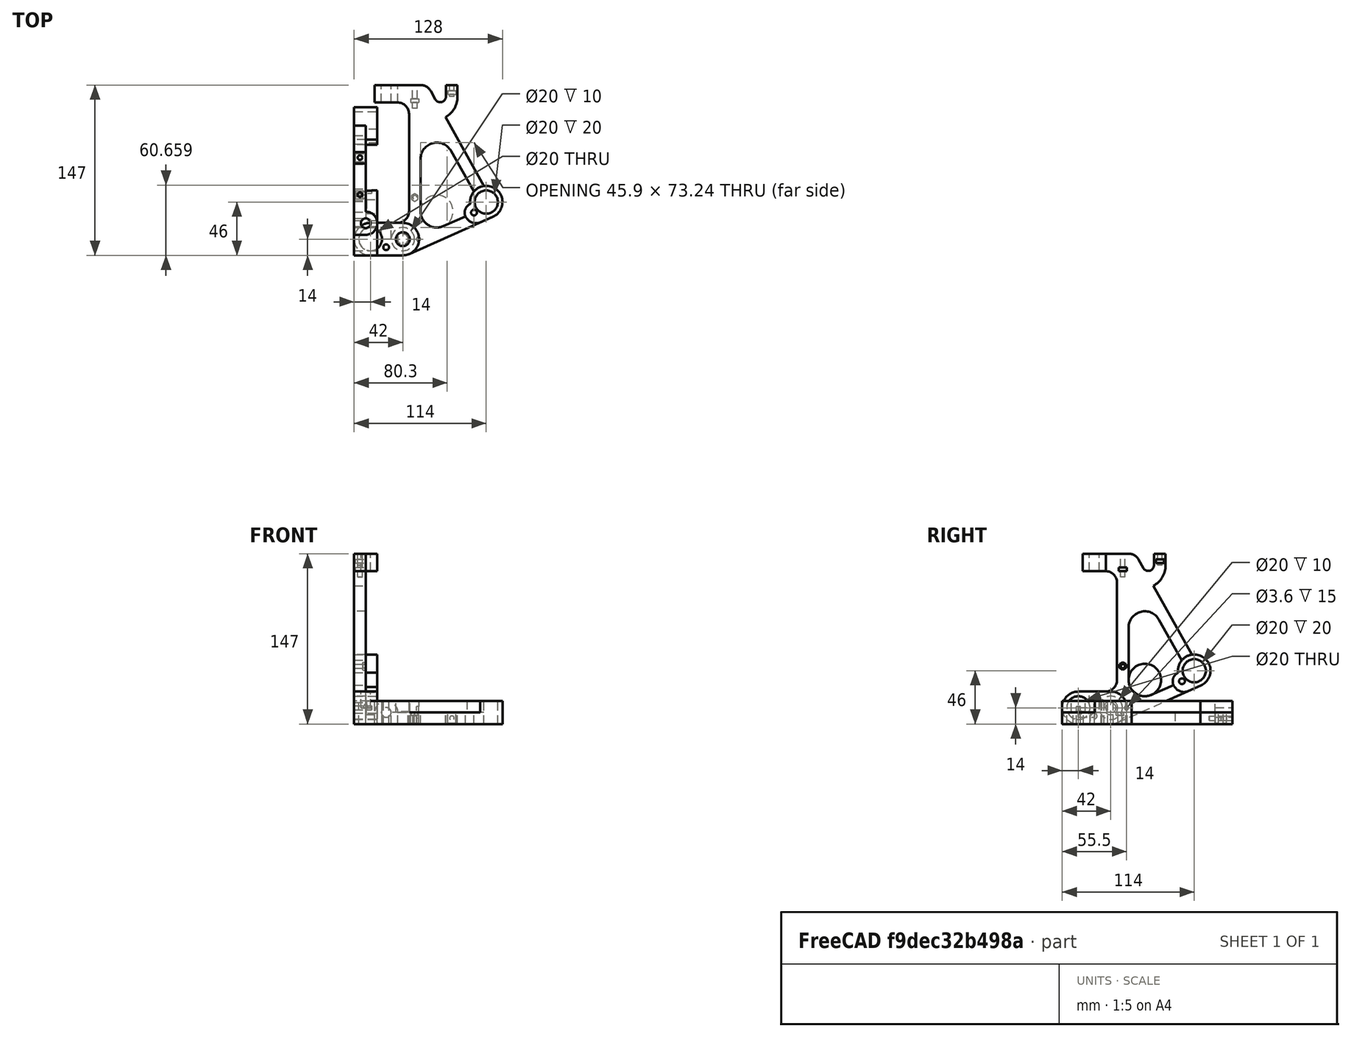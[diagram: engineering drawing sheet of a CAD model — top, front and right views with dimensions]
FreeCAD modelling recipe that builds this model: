
FCSTD DOCUMENT  (FreeCAD 0.15R4527 (Git))
Label: x_carriage_left
License: All rights reserved
LicenseURL: http://en.wikipedia.org/wiki/All_rights_reserved
objects: Part::Cylinder×14, Part::MultiFuse×10, Part::Cut×7, Part::Feature×2, Sketcher::SketchObject×2, Part::Box×2, Mesh::Feature×1, Part::Extrusion×1, PartDesign::Pocket×1, Part::Prism×1
note: 41 computed .brp shape members not serialized (recipe doc carries the construction recipe); baked Part::Feature solids carry a one-line shape summary decoded from their .brp

FEATURE [Mesh::Feature] Xcariageleft
FEATURE [Part::Feature] Xcariageleft001001  label="Xcariageleft002"
  shape: bbox 128 x 147 x 20 mm, 1927 faces, 0 solids (baked)
FEATURE [Sketcher::SketchObject] Sketch
  ExternalGeometry = -> [Xcariageleft001001]
  Placement = pos=(0,0,3.8147e-06) rot=(1,0,0;3.14159rad)
  Support = -> Xcariageleft001001 [Face866]
  sketch-geometry (27):
    g0: LineSegment StartX=14 StartY=-3e-12 StartZ=0 EndX=42 EndY=1e-12 EndZ=0
    g1: LineSegment StartX=47.6883 StartY=-1.20767 StartZ=0 EndX=119.688 EndY=-33.2233 EndZ=0
    g2: LineSegment StartX=111.977 StartY=-59.8687 StartZ=0 EndX=78.7678 EndY=-119.207 EndZ=0
    g3: LineSegment StartX=83.5669 StartY=-90.1556 StartZ=0 EndX=103.25 EndY=-54.9849 EndZ=0
    g4: LineSegment StartX=96.0562 StartY=-33.6591 StartZ=0 EndX=77.0383 EndY=-25.2025 EndZ=0
    g5: LineSegment StartX=57.35 StartY=-37.9949 StartZ=0 EndX=57.35 EndY=-83.3184 EndZ=0
    g6: LineSegment StartX=14 StartY=-28 StartZ=0 EndX=37.35 EndY=-28 EndZ=0
    g7: LineSegment StartX=47.35 StartY=-38 StartZ=0 EndX=47.35 EndY=-122 EndZ=0
    g8: LineSegment StartX=37.35 StartY=-132 StartZ=0 EndX=17.7 EndY=-132 EndZ=0
    g9: ArcOfCircle CenterX=114 CenterY=-46.0156 CenterZ=0 NormalX=0 NormalY=0 NormalZ=1 Radius=14 StartAngle=4.56737 EndAngle=7.43558
    g10: ArcOfCircle CenterX=103.366 CenterY=-36.9095 CenterZ=0 NormalX=0 NormalY=0 NormalZ=1 Radius=8.00001 StartAngle=2.72319 EndAngle=4.29398
    g11: ArcOfCircle CenterX=114 CenterY=-46.0156 CenterZ=0 NormalX=0 NormalY=0 NormalZ=1 Radius=14 StartAngle=3.01294 EndAngle=3.83695
    g12: ArcOfCircle CenterX=71.35 CenterY=-83.3184 CenterZ=0 NormalX=0 NormalY=0 NormalZ=1 Radius=14 StartAngle=3.14159 EndAngle=5.77296
    g13: ArcOfCircle CenterX=68.8096 CenterY=-137 CenterZ=0 NormalX=0 NormalY=0 NormalZ=1 Radius=20.3904 StartAngle=2.53065e-07 EndAngle=1.06057
    g14: ArcOfCircle CenterX=74.3581 CenterY=-137 CenterZ=0 NormalX=0 NormalY=0 NormalZ=1 Radius=4.84187 StartAngle=1.80253e-06 EndAngle=2.63136
    g15: ArcOfCircle CenterX=57.35 CenterY=-137 CenterZ=0 NormalX=0 NormalY=0 NormalZ=1 Radius=10 StartAngle=4.71239 EndAngle=5.77295
    g16: ArcOfCircle CenterX=37.35 CenterY=-122 CenterZ=0 NormalX=0 NormalY=0 NormalZ=1 Radius=10 StartAngle=4.71239 EndAngle=6.28318
    g17: ArcOfCircle CenterX=71.35 CenterY=-37.9949 CenterZ=0 NormalX=0 NormalY=0 NormalZ=1 Radius=14 StartAngle=1.15239 EndAngle=3.14159
    g18: ArcOfCircle CenterX=37.35 CenterY=-38 CenterZ=0 NormalX=0 NormalY=0 NormalZ=1 Radius=10 StartAngle=6.16e-10 EndAngle=1.5708
    g19: ArcOfCircle CenterX=42 CenterY=-13.9999 CenterZ=0 NormalX=0 NormalY=0 NormalZ=1 Radius=13.9999 StartAngle=1.15239 EndAngle=1.5708
    g20: ArcOfCircle CenterX=14 CenterY=-14 CenterZ=0 NormalX=0 NormalY=0 NormalZ=1 Radius=14 StartAngle=1.5708 EndAngle=4.71239
    g21: LineSegment StartX=17.7 StartY=-132 StartZ=0 EndX=17.7 EndY=-147 EndZ=0
    g22: LineSegment StartX=17.7 StartY=-147 StartZ=0 EndX=57.35 EndY=-147 EndZ=0
    g23: LineSegment StartX=70.133 StartY=-134.635 StartZ=0 EndX=66.0763 EndY=-141.884 EndZ=0
    g24: LineSegment StartX=79.2 StartY=-137 StartZ=0 EndX=79.2 EndY=-147 EndZ=0
    g25: LineSegment StartX=89.2 StartY=-137 StartZ=0 EndX=89.2 EndY=-147 EndZ=0
    g26: LineSegment StartX=79.2 StartY=-147 StartZ=0 EndX=89.2 EndY=-147 EndZ=0
  constraints (66):
    c: Coincident(g0,g-4)
    c: Coincident(g0,g-4)
    c: Coincident(g1,g-3)
    c: Coincident(g1,g-3)
    c: Coincident(g2,g-9)
    c: Coincident(g2,g-9)
    c: Coincident(g3,g-8)
    c: Coincident(g3,g-8)
    c: Coincident(g4,g-17)
    c: Coincident(g4,g-17)
    c: Coincident(g5,g-7)
    c: Coincident(g5,g-7)
    c: Coincident(g6,g-5)
    c: Coincident(g6,g-5)
    c: Coincident(g7,g-6)
    c: Coincident(g7,g-6)
    c: Coincident(g8,g-16)
    c: Coincident(g8,g-16)
    c: Coincident(g9,g2)
    c: Coincident(g9,g1)
    c: PointOnObject(g-22,g9)
    c: Coincident(g10,g-20)
    c: Coincident(g10,g4)
    c: PointOnObject(g-19,g10)
    c: Coincident(g11,g10)
    c: Coincident(g11,g3)
    c: PointOnObject(g-21,g11)
    c: Coincident(g12,g5)
    c: Coincident(g12,g3)
    c: PointOnObject(g-27,g12)
    c: Coincident(g13,g2)
    c: Coincident(g13,g-10)
    c: PointOnObject(g-23,g13)
    c: Coincident(g14,g-13)
    c: Coincident(g14,g-12)
    c: PointOnObject(g-24,g14)
    c: Coincident(g15,g-13)
    c: Coincident(g15,g-14)
    c: PointOnObject(g-25,g15)
    c: Coincident(g16,g8)
    c: Coincident(g16,g7)
    c: PointOnObject(g-26,g16)
    c: Coincident(g17,g5)
    c: Coincident(g17,g4)
    c: PointOnObject(g-18,g17)
    c: Coincident(g18,g7)
    c: Coincident(g18,g6)
    c: PointOnObject(g-28,g18)
    c: Coincident(g19,g1)
    c: Coincident(g19,g0)
    c: PointOnObject(g-30,g19)
    c: Coincident(g20,g6)
    c: Coincident(g20,g0)
    c: PointOnObject(g-29,g20)
    c: Coincident(g21,g8)
    c: Coincident(g21,g-15)
    c: Coincident(g22,g21)
    c: Coincident(g22,g15)
    c: Coincident(g23,g14)
    c: Coincident(g23,g15)
    c: Coincident(g24,g14)
    c: Coincident(g24,g-12)
    c: Coincident(g25,g13)
    c: Coincident(g25,g-11)
    c: Coincident(g26,g24)
    c: Coincident(g26,g25)
FEATURE [Part::Cylinder] Cylinder  label="Cilindro"
  Angle = 360
  Height = 15
  Placement = pos=(27.7,132,10) rot=(-1,0,0;1.5708rad)
  Radius = 10
FEATURE [Part::Cylinder] Cylinder001  label="rod_hole"
  Angle = 360
  Height = 15
  Placement = pos=(27.7,132,10) rot=(-1,0,0;1.5708rad)
  Radius = 4.2
FEATURE [Part::Cylinder] Cylinder002  label="Cilindro001"
  Angle = 360
  Height = 22
  Placement = pos=(14,14,-1) rot=(0,0,1;0rad)
  Radius = 10
FEATURE [Part::Cylinder] Cylinder003  label="Cilindro002"
  Angle = 360
  Height = 22
  Placement = pos=(114,46,-1) rot=(0,0,1;0rad)
  Radius = 10
FEATURE [Part::Cylinder] Cylinder004  label="Cilindro003"
  Angle = 360
  Height = 10
  Placement = pos=(42,14,10.6) rot=(0,0,1;0rad)
  Radius = 6
FEATURE [Part::Cylinder] Cylinder005  label="Cilindro004"
  Angle = 360
  Height = 11
  Placement = pos=(42,14,-1) rot=(0,0,1;0rad)
  Radius = 10
FEATURE [Part::Cylinder] Cylinder006  label="threaded_rod"
  Angle = 360
  Height = 10
  Placement = pos=(42,14,0) rot=(0,0,1;0rad)
  Radius = 4.5
FEATURE [Part::MultiFuse] Fusion003  label="bearing_holes"
  Shapes = -> [Cylinder002,Cylinder003]
FEATURE [Part::MultiFuse] Fusion004  label="threaded_rod_holes"
  Shapes = -> [Cylinder004,Cylinder005]
FEATURE [Part::Extrusion] Extrude
  Base = -> Sketch
  Dir = (0,0,20)
  Solid = true
FEATURE [Sketcher::SketchObject] Sketch001
  ExternalGeometry = -> [Extrude]
  Placement = pos=(0,0,20) rot=(0,0,1;0rad)
  Support = -> Extrude [Face29]
  sketch-geometry (31):
    g0: LineSegment StartX=37.35 StartY=132 StartZ=0 EndX=17.7 EndY=132 EndZ=0
    g1: LineSegment StartX=17.7 StartY=132 StartZ=0 EndX=17.7 EndY=147 EndZ=0
    g2: LineSegment StartX=17.7 StartY=147 StartZ=0 EndX=57.35 EndY=147 EndZ=0
    g3: LineSegment StartX=79.2 StartY=137 StartZ=0 EndX=79.2 EndY=147 EndZ=0
    g4: LineSegment StartX=89.2 StartY=147 StartZ=0 EndX=89.2 EndY=137 EndZ=0
    g5: ArcOfCircle CenterX=57.35 CenterY=137 CenterZ=0 NormalX=0 NormalY=0 NormalZ=1 Radius=10 StartAngle=0.510231 EndAngle=1.5708
    g6: ArcOfCircle CenterX=68.8096 CenterY=137 CenterZ=0 NormalX=0 NormalY=0 NormalZ=1 Radius=20.3904 StartAngle=5.22262 EndAngle=6.28319
    g7: ArcOfCircle CenterX=74.3581 CenterY=137 CenterZ=0 NormalX=0 NormalY=0 NormalZ=1 Radius=4.84187 StartAngle=3.65182 EndAngle=6.28318
    g8: LineSegment StartX=66.0763 StartY=141.884 StartZ=0 EndX=70.133 EndY=134.635 EndZ=0
    g9: ArcOfCircle CenterX=37.35 CenterY=122 CenterZ=0 NormalX=0 NormalY=0 NormalZ=1 Radius=10 StartAngle=1.08019e-06 EndAngle=1.5708
    g10: LineSegment StartX=79.2 StartY=147 StartZ=0 EndX=89.2 EndY=147 EndZ=0
    g11: LineSegment StartX=47.35 StartY=122 StartZ=0 EndX=47.35 EndY=38 EndZ=0
    g12: LineSegment StartX=57.35 StartY=83.3184 StartZ=0 EndX=57.35 EndY=37.9949 EndZ=0
    g13: ArcOfCircle CenterX=71.35 CenterY=83.3184 CenterZ=0 NormalX=0 NormalY=0 NormalZ=1 Radius=14 StartAngle=0.510228 EndAngle=3.14159
    g14: LineSegment StartX=83.5669 StartY=90.1556 StartZ=0 EndX=103.25 EndY=54.9849 EndZ=0
    g15: LineSegment StartX=77.0383 StartY=25.2025 StartZ=0 EndX=96.0562 EndY=33.6591 EndZ=0
    g16: LineSegment [constr] StartX=57.35 StartY=37.9949 StartZ=0 EndX=71.35 EndY=37.9949 EndZ=0
    g17: LineSegment [constr] StartX=71.35 StartY=37.9949 StartZ=0 EndX=77.0383 EndY=25.2025 EndZ=0
    g18: ArcOfCircle CenterX=71.35 CenterY=37.9949 CenterZ=0 NormalX=0 NormalY=0 NormalZ=1 Radius=14 StartAngle=3.14159 EndAngle=5.13079
    g19: LineSegment [constr] StartX=111.977 StartY=59.8687 StartZ=0 EndX=114 EndY=46.0156 EndZ=0
    g20: ArcOfCircle CenterX=114 CenterY=46.0156 CenterZ=0 NormalX=0 NormalY=0 NormalZ=1 Radius=14 StartAngle=1.71582 EndAngle=2.44623
    g21: LineSegment [constr] StartX=103.366 StartY=36.9095 StartZ=0 EndX=96.0562 EndY=33.6591 EndZ=0
    g22: LineSegment StartX=111.977 StartY=59.8687 StartZ=0 EndX=78.7678 EndY=119.207 EndZ=0
    g23: LineSegment [constr] StartX=119.688 StartY=33.2233 StartZ=0 EndX=108.723 EndY=28.3476 EndZ=0
    g24: ArcOfCircle CenterX=41.9997 CenterY=13.9999 CenterZ=0 NormalX=0 NormalY=0 NormalZ=1 Radius=14.0001 StartAngle=5.13081 EndAngle=7.85396
    g25: LineSegment StartX=37.35 StartY=28 StartZ=0 EndX=42 EndY=28 EndZ=0
    g26: LineSegment [constr] StartX=37.35 StartY=28 StartZ=0 EndX=41.9997 EndY=13.9999 EndZ=0
    g27: ArcOfCircle CenterX=37.35 CenterY=38 CenterZ=0 NormalX=0 NormalY=0 NormalZ=1 Radius=10 StartAngle=4.71239 EndAngle=6.28319
    g28: LineSegment StartX=47.6883 StartY=1.20767 StartZ=0 EndX=108.723 EndY=28.3476 EndZ=0
    g29: ArcOfCircle CenterX=103.366 CenterY=36.9095 CenterZ=0 NormalX=0 NormalY=0 NormalZ=1 Radius=8 StartAngle=3.56 EndAngle=3.8283
    g30: ArcOfCircle CenterX=105.144 CenterY=37.344 CenterZ=0 NormalX=0 NormalY=0 NormalZ=1 Radius=9.68242 StartAngle=3.74652 EndAngle=5.09109
  constraints (78):
    c: Coincident(g0,g-14)
    c: Coincident(g0,g-5)
    c: Coincident(g1,g0)
    c: Coincident(g1,g-6)
    c: Coincident(g2,g1)
    c: Coincident(g2,g-8)
    c: Coincident(g3,g-10)
    c: Coincident(g3,g-11)
    c: Coincident(g4,g-12)
    c: Coincident(g4,g-13)
    c: Coincident(g5,g-8)
    c: Coincident(g5,g2)
    c: Coincident(g5,g-8)
    c: Coincident(g6,g-13)
    c: Coincident(g6,g4)
    c: Coincident(g6,g-15)
    c: Coincident(g7,g-9)
    c: Coincident(g7,g-9)
    c: Coincident(g7,g3)
    c: Coincident(g8,g5)
    c: Coincident(g8,g7)
    c: Coincident(g9,g-14)
    c: Coincident(g9,g0)
    c: Coincident(g9,g-14)
    c: Coincident(g10,g3)
    c: Coincident(g10,g4)
    c: Coincident(g11,g9)
    c: Coincident(g11,g-19)
    c: Coincident(g12,g-18)
    c: Coincident(g13,g-17)
    c: Coincident(g13,g12)
    c: Coincident(g13,g-17)
    c: Coincident(g14,g13)
    c: Coincident(g15,g-21)
    c: Coincident(g16,g12)
    c: Horizontal(g16)
    c: Coincident(g17,g16)
    c: Coincident(g17,g15)
    c: DistanceX(g16) = 14
    c: Equal(g16,g17)
    c: Vertical(g12)
    c: Coincident(g18,g16)
    c: Coincident(g18,g12)
    c: Coincident(g18,g15)
    c: Distance(g19) = 14
    c: Coincident(g20,g19)
    c: Coincident(g20,g19)
    c: Coincident(g19,g-15)
    c: Coincident(g21,g15)
    c: Parallel(g21,g-21)
    c: Distance(g21) = 8
    c: Coincident(g15,g-21)
    c: Coincident(g14,g-16)
    c: Coincident(g22,g19)
    c: Coincident(g22,g6)
    c: Coincident(g23,g-20)
    c: Distance(g23) = 12
    c: PointOnObject(g23,g-20)
    c: Coincident(g25,g-19)
    c: Coincident(g25,g24)
    c: Horizontal(g25)
    c: DistanceX(g25) = 4.65003
    c: Coincident(g26,g25)
    c: Coincident(g26,g24)
    c: Distance(g26) = 14.752
    c: Coincident(g24,g-20)
    c: Coincident(g27,g-19)
    c: Coincident(g27,g25)
    c: Coincident(g27,g11)
    c: Coincident(g28,g24)
    c: Coincident(g28,g23)
    c: Coincident(g29,g21)
    c: Coincident(g29,g15)
    c: Coincident(g30,g23)
    c: Coincident(g29,g30)
    c: Angle(g29) = 0.268297
    c: Coincident(g20,g14)
    c: Angle(g30) = 1.34458
FEATURE [PartDesign::Pocket] Pocket
  Length = 10
  Sketch = -> Sketch001
  Type = 0
FEATURE [Part::MultiFuse] Fusion
  Shapes = -> [Pocket,Cylinder]
FEATURE [Part::Cut] Cut
  Base = -> Fusion
  Tool = -> Fusion004
FEATURE [Part::MultiFuse] Fusion005
  Shapes = -> [Cut,Cylinder006]
FEATURE [Part::Cylinder] Cylinder007  label="Cilindro005"
  Angle = 360
  Height = 22
  Placement = pos=(27.6,7,-1) rot=(0,0,1;0rad)
  Radius = 2.5
FEATURE [Part::Cylinder] Cylinder008  label="Cilindro006"
  Angle = 360
  Height = 22
  Placement = pos=(103.4,36.9,-1) rot=(0,0,1;0rad)
  Radius = 2.5
FEATURE [Part::Cylinder] Cylinder009  label="rod_hole001"
  Angle = 360
  Height = 15
  Placement = pos=(27.7,14,10) rot=(-1,0,0;1.5708rad)
  Radius = 4.2
FEATURE [Part::Cut] Cut001
  Base = -> Fusion005
  Tool = -> Fusion003
FEATURE [Part::MultiFuse] Fusion006  label="rod_holes"
  Shapes = -> [Cylinder009,Cylinder001]
FEATURE [Part::Cut] Cut002
  Base = -> Cut001
  Tool = -> Fusion006
FEATURE [Part::MultiFuse] Fusion007  label="joined_holes"
  Shapes = -> [Cylinder008,Cylinder007]
FEATURE [Part::Cut] Cut003
  Base = -> Cut002
  Tool = -> Fusion007
FEATURE [Part::Cylinder] Cylinder010  label="Cilindro007"
  Angle = 360
  Height = 21
  Placement = pos=(52.35,127,5) rot=(-1,0,0;1.5708rad)
  Radius = 2
FEATURE [Part::Cylinder] Cylinder011  label="Cilindro008"
  Angle = 360
  Height = 11
  Placement = pos=(84.35,137,5) rot=(-1,0,0;1.5708rad)
  Radius = 2
FEATURE [Part::MultiFuse] Fusion008  label="screw_holes"
  Shapes = -> [Cylinder010,Cylinder011]
FEATURE [Part::Box] Box  label="Cubo"
  Height = 10
  Length = 7
  Placement = pos=(48.8,132,1) rot=(0,0,1;0rad)
  Width = 3
FEATURE [Part::Box] Box001  label="Cubo001"
  Height = 10
  Length = 7
  Placement = pos=(80.8,139,1) rot=(0,0,1;0rad)
  Width = 3
FEATURE [Part::MultiFuse] Fusion009  label="nut_holes"
  Shapes = -> [Box,Box001]
FEATURE [Part::MultiFuse] Fusion010  label="screws_top"
  Shapes = -> [Fusion008,Fusion009]
FEATURE [Part::Cut] Cut004
  Base = -> Cut003
  Tool = -> Fusion010
FEATURE [Part::Cylinder] Cylinder012  label="Cilindro009"
  Angle = 360
  Height = 15
  Placement = pos=(55.5,14,0) rot=(0,0,1;0rad)
  Radius = 1.8
FEATURE [Part::Cut] Cut005
  Base = -> Cut004
  Tool = -> Cylinder012
FEATURE [Part::Cylinder] Cylinder013  label="Cilindro010"
  Angle = 360
  Height = 11
  Placement = pos=(52.35,50,-1) rot=(0,0,1;0rad)
  Radius = 1.8
FEATURE [Part::Prism] Prism  label="Prisma"
  Circumradius = 3.3
  Height = 3
  Placement = pos=(52.35,50,7.5) rot=(0,0,1;0.523599rad)
  Polygon = 6
FEATURE [Part::MultiFuse] Fusion011  label="precision_screw"
  Shapes = -> [Cylinder013,Prism]
FEATURE [Part::Cut] Cut006  label="x_carriage_left"
  Base = -> Cut005
  Tool = -> Fusion011
FEATURE [Part::Feature] Cut007  label="x_carriage_left001"
  Placement = pos=(0,0,0) rot=(0.57735,0.57735,0.57735;2.0944rad)
  shape: bbox 20 x 128 x 147 mm, 78 faces (baked)
